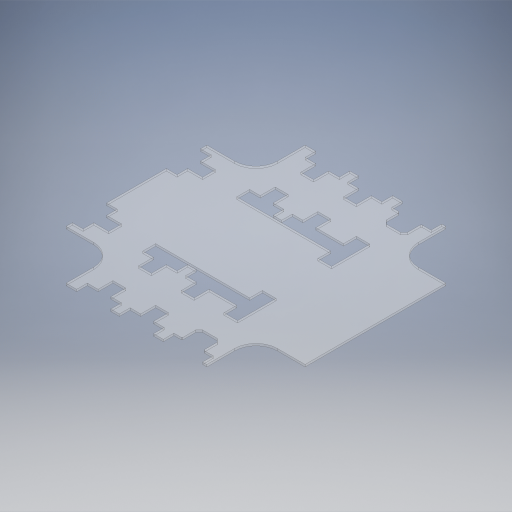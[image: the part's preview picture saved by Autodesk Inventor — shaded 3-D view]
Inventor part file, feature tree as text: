
AUTODESK INVENTOR PART (.ipt)
format: ipt  version: 2024.2 (Build 282272000, 272)  size: 730,112 bytes
history: native  units: in
note: dims shown in document units (in); Inventor stores cm internally (conversion verified against a paired STEP export)
features: extrude x8, sketch x8, projected_geometry x7
ambient origin geometry x8: Origin, YZ Plane, XZ Plane, XY Plane, X Axis, Y Axis, Z Axis, Center Point
bodies: Solid1 (feature_tree)
feature tree (23):
  extrude  "Extrusion1"  Depth=28.0in
  extrude  "Extrusion2"  Depth=3.0in
  extrude  "Extrusion3"  Depth=1.75in
  extrude  "Extrusion4"  Depth=0.25in TaperAngle=0.0deg
  extrude  "Extrusion5"  Depth=1.25in
  extrude  "Extrusion6"  Depth=1.75in
  extrude  "Extrusion7"  Depth=1.25in
  extrude  "Extrusion8"  Depth=5.75in
  sketch  "Sketch1"  dims[d0=28.0in d1=28.0in]
  sketch  "Sketch2"  dims[d2=0.25in d3=0.0in d4=3.0in]
  projected_geometry  "Projected Loop1"
  sketch  "Sketch3"  dims[d5=1.25in d6=1.75in]
  projected_geometry  "Projected Loop2"
  sketch  "Sketch4"  dims[d7=1.75in d8=0.25in d9=0.0in]
  projected_geometry  "Projected Loop3"
  sketch  "Sketch5"  dims[d10=6.5in d11=1.25in]
  projected_geometry  "Projected Loop4"
  sketch  "Sketch6"  dims[d12=1.25in d13=1.75in]
  projected_geometry  "Projected Loop5"
  sketch  "Sketch7"  dims[d14=1.5in d15=1.25in]
  projected_geometry  "Projected Loop6"
  sketch  "Sketch8"  dims[d16=0.25in d17=0.0in d18=5.75in d19=5.75in d20=2.5in d21=0.25in d22=0.0in d24=6.25in d25=1.25in d26=1.25in d27=1.05in d30=1.5in d33=1.707in d34=0.846in d35=22.6875in d36=0.0in d38=6.625in d39=14.375in d40=0.0in d42=0.25in d43=0.25in d44=0.5in d45=1.25in d46=1.147in d47=1.25in d48=1.75in d49=1.5in d50=1.75in d51=1.25in d52=0.5in d53=0.5in d54=14.375in d55=0.0in d56=1.5in d57=1.0in d58=0.0in]
  projected_geometry  "Projected Loop7"
